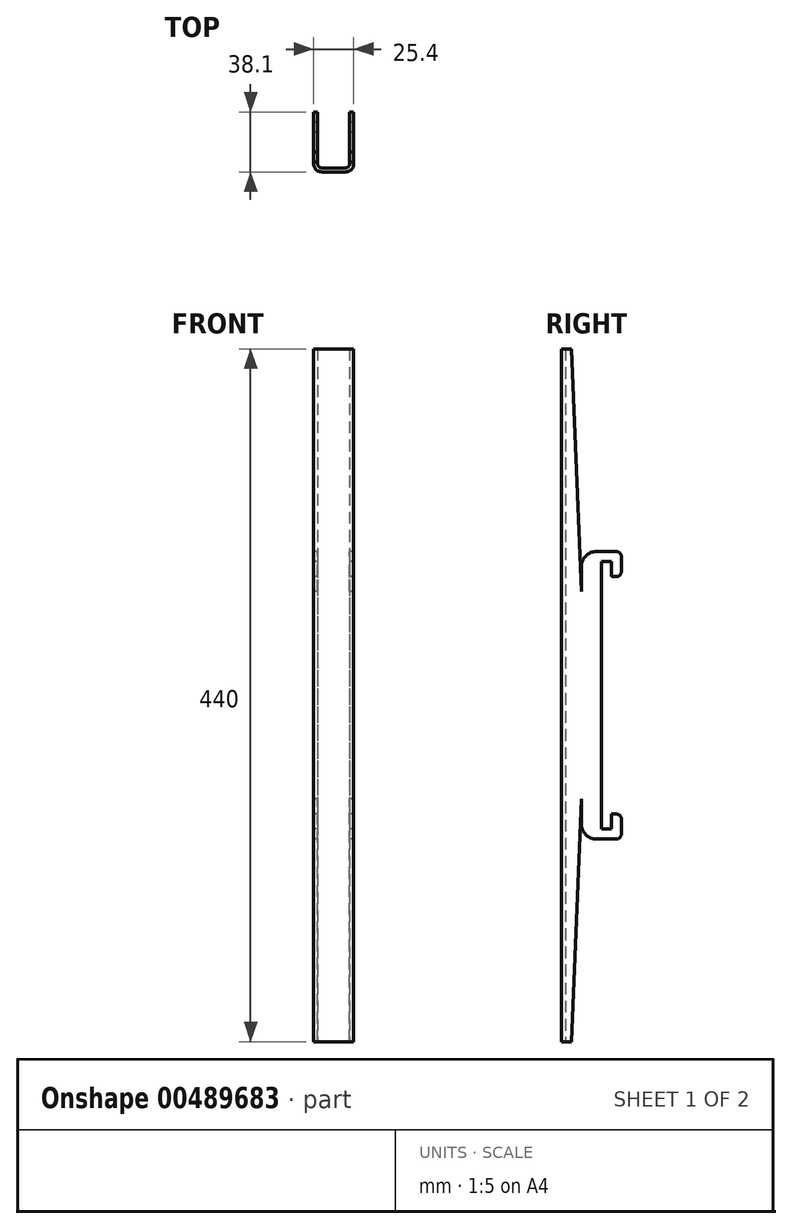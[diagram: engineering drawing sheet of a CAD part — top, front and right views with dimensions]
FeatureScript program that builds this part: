
annotation { "Feature Type Name" : "Feature", "Feature Type Description" : "" }
export const myFeature = defineFeature(function(context is Context, id is Id, definition is map)
    precondition{}
    {
        {
            var Q0;
            Q0=qCreatedBy(makeId("Right.planeOp"),FACE);
            var sketch = newSketch(context, id + "F0", { "sketchPlane" : qUnion([Q0])});
            skLineSegment(sketch, "E0", {"start": v(-31.75, 220) * mm, "end": v(-31.75, -220) * mm});
            skLineSegment(sketch, "E1", {"start": v(-31.75, -220) * mm, "end": v(-25.4, -220) * mm});
            skLineSegment(sketch, "E2", {"start": v(-25.4, -220) * mm, "end": v(-19.05, -65.95) * mm});
            skLineSegment(sketch, "E3", {"start": v(-19.05, -65.95) * mm, "end": v(-19.05, -81.7) * mm});
            skLineSegment(sketch, "E4", {"start": v(-9.4, -91.35) * mm, "end": v(3.05, -91.35) * mm});
            skLineSegment(sketch, "E5", {"start": v(6.35, -88.05) * mm, "end": v(6.35, -78.65) * mm});
            skLineSegment(sketch, "E6", {"start": v(3.05, -75.35) * mm, "end": v(0, -75.35) * mm});
            skLineSegment(sketch, "E7", {"start": v(0, -75.35) * mm, "end": v(0, -85) * mm});
            skLineSegment(sketch, "E8", {"start": v(0, -85) * mm, "end": v(-6.35, -85) * mm});
            skLineSegment(sketch, "E9.MirrorCS", {"start": v(3.05, 75.35) * mm, "end": v(0, 75.35) * mm});
            skLineSegment(sketch, "E10.MirrorCS", {"start": v(-31.75, 220) * mm, "end": v(-25.4, 220) * mm});
            skLineSegment(sketch, "E11.MirrorCS", {"start": v(0, 85) * mm, "end": v(-6.35, 85) * mm});
            skLineSegment(sketch, "E12.MirrorCS", {"start": v(0, 75.35) * mm, "end": v(0, 85) * mm});
            skLineSegment(sketch, "E13.MirrorCS", {"start": v(-25.4, 220) * mm, "end": v(-19.05, 65.95) * mm});
            skLineSegment(sketch, "E14.MirrorCS", {"start": v(6.35, 88.05) * mm, "end": v(6.35, 78.65) * mm});
            skLineSegment(sketch, "E15.MirrorCS", {"start": v(-9.4, 91.35) * mm, "end": v(3.05, 91.35) * mm});
            skLineSegment(sketch, "E16.MirrorCS", {"start": v(-19.05, 65.95) * mm, "end": v(-19.05, 81.7) * mm});
            skLineSegment(sketch, "E17", {"start": v(-6.35, 85) * mm, "end": v(-6.35, -85) * mm});
            skPoint(sketch, "E18.visualSharp", {"position": v(-19.05, -91.35) * mm});
            skArc(sketch, "E18.filletArc", {"start": v(-19.05, -81.7) * mm, "mid": v(-16.22, -88.52) * mm, "end": v(-9.4, -91.35) * mm});
            skPoint(sketch, "E19.visualSharp", {"position": v(-19.05, 91.35) * mm});
            skArc(sketch, "E19.filletArc", {"start": v(-9.4, 91.35) * mm, "mid": v(-16.22, 88.52) * mm, "end": v(-19.05, 81.7) * mm});
            skPoint(sketch, "E20.visualSharp", {"position": v(6.35, -91.35) * mm});
            skArc(sketch, "E20.filletArc", {"start": v(3.05, -91.35) * mm, "mid": v(5.38, -90.38) * mm, "end": v(6.35, -88.05) * mm});
            skPoint(sketch, "E21.visualSharp", {"position": v(6.35, -75.35) * mm});
            skArc(sketch, "E21.filletArc", {"start": v(6.35, -78.65) * mm, "mid": v(5.38, -76.32) * mm, "end": v(3.05, -75.35) * mm});
            skPoint(sketch, "E22.visualSharp", {"position": v(6.35, 91.35) * mm});
            skArc(sketch, "E22.filletArc", {"start": v(6.35, 88.05) * mm, "mid": v(5.38, 90.38) * mm, "end": v(3.05, 91.35) * mm});
            skPoint(sketch, "E23.visualSharp", {"position": v(6.35, 75.35) * mm});
            skArc(sketch, "E23.filletArc", {"start": v(3.05, 75.35) * mm, "mid": v(5.38, 76.32) * mm, "end": v(6.35, 78.65) * mm});
            skSolve(sketch);
        }
        {
            var Q0;
            Q0=makeQuery(id+"F0.imprint","IMPRINT",FACE,{"disambiguationData":[TD([[makeQuery(id+"F0.imprint","IMPRINT",EDGE,{"derivedFrom":sQuery(id+"F0.wireOp",EDGE,"E0")}),1.0]])]});
            extrude(context, id + "F1", {"entities" : qUnion([Q0]), "endBound" : BoundingType.SYMMETRIC, "depth" : 25.4 * mm});
        }
        {
            var Q0;
            Q0=makeQuery(id+"F1.opExtrude","CAP_EDGE",EDGE,{"disambiguationData":[OSD([sQuery(id+"F0.wireOp",EDGE,"E0")])],"isStart":false});
            var Q1;
            Q1=makeQuery(id+"F1.opExtrude","CAP_EDGE",EDGE,{"disambiguationData":[OSD([sQuery(id+"F0.wireOp",EDGE,"E0")])],"isStart":true});
            fillet(context, id + "F2", {"entities" : qUnion([Q0, Q1]), "radius" : 5.08 * mm, "tangentPropagation" : true, "allowEdgeOverflow" : false});
        }
        {
            var Q0;
            Q0=qCreatedBy(makeId("Top.planeOp"),FACE);
            var sketch = newSketch(context, id + "F3", { "sketchPlane" : qUnion([Q0])});
            skLineSegment(sketch, "E24.bottom", {"start": v(10.16, 6.35) * mm, "end": v(-10.16, 6.35) * mm});
            skLineSegment(sketch, "E24.top", {"start": v(7.62, -29.2) * mm, "end": v(-7.62, -29.2) * mm});
            skLineSegment(sketch, "E24.left", {"start": v(10.16, 6.35) * mm, "end": v(10.16, -26.67) * mm});
            skLineSegment(sketch, "E24.right", {"start": v(-10.16, 6.35) * mm, "end": v(-10.16, -26.67) * mm});
            skPoint(sketch, "E25.visualSharp", {"position": v(10.16, -29.2) * mm});
            skArc(sketch, "E25.filletArc", {"start": v(7.62, -29.2) * mm, "mid": v(9.42, -28.47) * mm, "end": v(10.16, -26.67) * mm});
            skPoint(sketch, "E26.visualSharp", {"position": v(-10.16, -29.2) * mm});
            skArc(sketch, "E26.filletArc", {"start": v(-10.16, -26.67) * mm, "mid": v(-9.42, -28.47) * mm, "end": v(-7.62, -29.2) * mm});
            skSolve(sketch);
        }
        {
            var Q0;
            Q0 = qSketchRegion(id + "F3", true);
            extrude(context, id + "F4", {"entities" : qUnion([Q0]), "operationType" : NewBodyOperationType.REMOVE, "endBound" : BoundingType.THROUGH_ALL, "depth" : 25.4 * mm, "hasSecondDirection" : true, "secondDirectionBound" : SecondDirectionBoundingType.THROUGH_ALL, "secondDirectionOppositeDirection" : true, "secondDirectionDepth" : 25.4 * mm});
        }
    });
